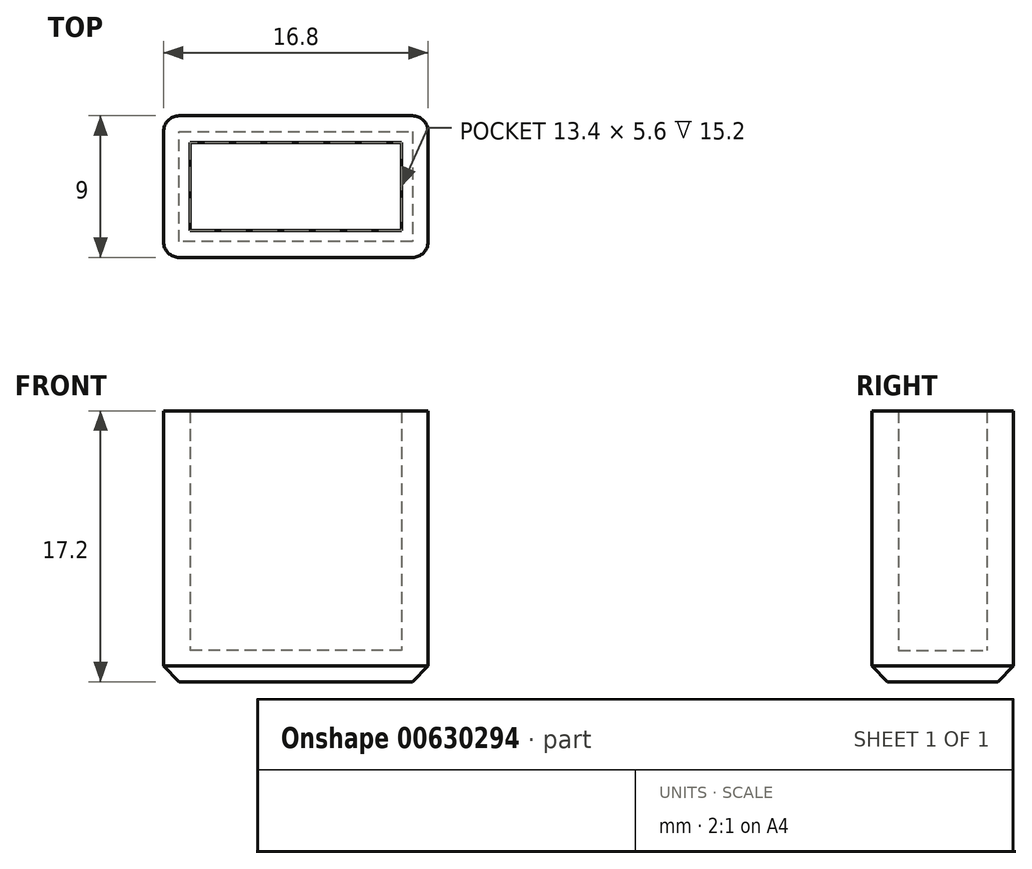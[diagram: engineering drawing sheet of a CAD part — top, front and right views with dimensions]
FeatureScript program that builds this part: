
annotation { "Feature Type Name" : "Feature", "Feature Type Description" : "" }
export const myFeature = defineFeature(function(context is Context, id is Id, definition is map)
    precondition{}
    {
        {
            var Q0;
            Q0=qCreatedBy(makeId("Top.planeOp"),FACE);
            var sketch = newSketch(context, id + "F0", { "sketchPlane" : qUnion([Q0])});
            skLineSegment(sketch, "E0.bottom", {"start": v(6.7, -2.8) * mm, "end": v(-6.7, -2.8) * mm});
            skLineSegment(sketch, "E0.top", {"start": v(6.7, 2.8) * mm, "end": v(-6.7, 2.8) * mm});
            skLineSegment(sketch, "E0.left", {"start": v(6.7, -2.8) * mm, "end": v(6.7, 2.8) * mm});
            skLineSegment(sketch, "E0.right", {"start": v(-6.7, -2.8) * mm, "end": v(-6.7, 2.8) * mm});
            skPoint(sketch, "E0.middle", {"position": v(0, 0) * mm});
            skLineSegment(sketch, "E1.bottom", {"start": v(8.4, -4.5) * mm, "end": v(-8.4, -4.5) * mm});
            skLineSegment(sketch, "E1.top", {"start": v(8.4, 4.5) * mm, "end": v(-8.4, 4.5) * mm});
            skLineSegment(sketch, "E1.left", {"start": v(8.4, -4.5) * mm, "end": v(8.4, 4.5) * mm});
            skLineSegment(sketch, "E1.right", {"start": v(-8.4, -4.5) * mm, "end": v(-8.4, 4.5) * mm});
            skSolve(sketch);
        }
        {
            var Q0;
            Q0=makeQuery(id+"F0.imprint","IMPRINT",FACE,{"disambiguationData":[TD([[makeQuery(id+"F0.imprint","IMPRINT",EDGE,{"derivedFrom":sQuery(id+"F0.wireOp",EDGE,"E0.bottom")}),1.0]])]});
            extrude(context, id + "F1", {"entities" : qUnion([Q0]), "depth" : 15.2 * mm, "offsetDistance" : 25 * mm});
        }
        {
            var Q0;
            Q0=makeQuery(id+"F0.imprint","IMPRINT",FACE,{"disambiguationData":[TD([[makeQuery(id+"F0.imprint","IMPRINT",EDGE,{"derivedFrom":sQuery(id+"F0.wireOp",EDGE,"E0.bottom")}),-1.0]])]});
            var Q1;
            Q1=makeQuery(id+"F0.imprint","IMPRINT",FACE,{"disambiguationData":[TD([[makeQuery(id+"F0.imprint","IMPRINT",EDGE,{"derivedFrom":sQuery(id+"F0.wireOp",EDGE,"E0.bottom")}),1.0]])]});
            extrude(context, id + "F2", {"entities" : qUnion([Q0, Q1]), "operationType" : NewBodyOperationType.ADD, "oppositeDirection" : true, "depth" : 2 * mm, "offsetDistance" : 25 * mm});
        }
        {
            var Q0;
            {var subQ0=sQuery(id+"F0.wireOp",EDGE,"E1.right");var subQ1=sQuery(id+"F0.wireOp",EDGE,"E1.top");Q0=makeQuery(id+"F2.boolean.opBoolean","MERGE",EDGE,{"derivedFrom":[makeQuery(id+"F1.opExtrude","SWEPT_EDGE",EDGE,{"disambiguationData":[OSD([subQ1,subQ0])]}),makeQuery(id+"F2.opExtrude","SWEPT_EDGE",EDGE,{"disambiguationData":[OSD([subQ1,subQ0])]})]});}
            var Q1;
            {var subQ0=sQuery(id+"F0.wireOp",EDGE,"E1.right");var subQ1=sQuery(id+"F0.wireOp",EDGE,"E1.bottom");Q1=makeQuery(id+"F2.boolean.opBoolean","MERGE",EDGE,{"derivedFrom":[makeQuery(id+"F1.opExtrude","SWEPT_EDGE",EDGE,{"disambiguationData":[OSD([subQ1,subQ0])]}),makeQuery(id+"F2.opExtrude","SWEPT_EDGE",EDGE,{"disambiguationData":[OSD([subQ1,subQ0])]})]});}
            var Q2;
            {var subQ0=sQuery(id+"F0.wireOp",EDGE,"E1.left");var subQ1=sQuery(id+"F0.wireOp",EDGE,"E1.bottom");Q2=makeQuery(id+"F2.boolean.opBoolean","MERGE",EDGE,{"derivedFrom":[makeQuery(id+"F1.opExtrude","SWEPT_EDGE",EDGE,{"disambiguationData":[OSD([subQ1,subQ0])]}),makeQuery(id+"F2.opExtrude","SWEPT_EDGE",EDGE,{"disambiguationData":[OSD([subQ1,subQ0])]})]});}
            var Q3;
            {var subQ0=sQuery(id+"F0.wireOp",EDGE,"E1.left");var subQ1=sQuery(id+"F0.wireOp",EDGE,"E1.top");Q3=makeQuery(id+"F2.boolean.opBoolean","MERGE",EDGE,{"derivedFrom":[makeQuery(id+"F1.opExtrude","SWEPT_EDGE",EDGE,{"disambiguationData":[OSD([subQ1,subQ0])]}),makeQuery(id+"F2.opExtrude","SWEPT_EDGE",EDGE,{"disambiguationData":[OSD([subQ1,subQ0])]})]});}
            fillet(context, id + "F3", {"entities" : qUnion([Q0, Q1, Q2, Q3]), "radius" : 1 * mm, "tangentPropagation" : true, "allowEdgeOverflow" : false});
        }
        {
            var Q0;
            Q0=makeQuery(id+"F2.opExtrude","CAP_FACE",FACE,{"disambiguationData":[OSD([sQuery(id+"F0.wireOp",EDGE,"E1.bottom"),sQuery(id+"F0.wireOp",EDGE,"E1.top"),sQuery(id+"F0.wireOp",EDGE,"E1.left"),sQuery(id+"F0.wireOp",EDGE,"E1.right")])],"isStart":false});
            chamfer(context, id + "F4", {"entities" : qUnion([Q0]), "width" : 1 * mm, "tangentPropagation" : true});
        }
    });
